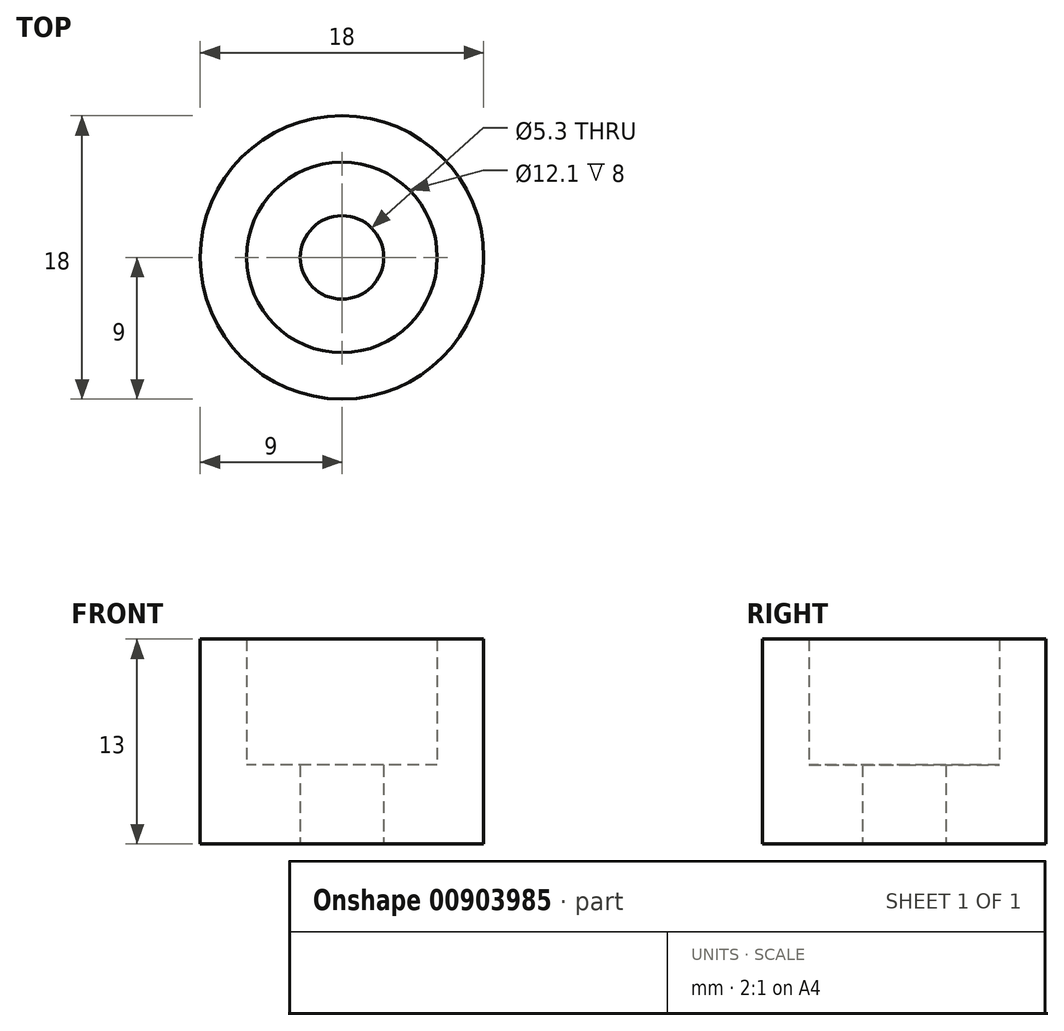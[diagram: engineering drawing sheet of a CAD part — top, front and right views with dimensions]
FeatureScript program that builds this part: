
annotation { "Feature Type Name" : "Feature", "Feature Type Description" : "" }
export const myFeature = defineFeature(function(context is Context, id is Id, definition is map)
    precondition{}
    {
        {
            var Q0;
            Q0=qCreatedBy(makeId("Top.planeOp"),FACE);
            var sketch = newSketch(context, id + "F0", { "sketchPlane" : qUnion([Q0])});
            skCircle(sketch, "E0", {"center": v(0, 0) * mm, "radius": 9 * mm});
            skCircle(sketch, "E1", {"center": v(0, 0) * mm, "radius": 6.05 * mm});
            skCircle(sketch, "E2", {"center": v(0, 0) * mm, "radius": 10 * mm});
            skCircle(sketch, "E3", {"center": v(0, 0) * mm, "radius": 2.65 * mm});
            skSolve(sketch);
        }
        {
            var Q0;
            Q0=makeQuery(id+"F0.imprint","IMPRINT",FACE,{"disambiguationData":[TD([[makeQuery(id+"F0.imprint","IMPRINT",EDGE,{"derivedFrom":sQuery(id+"F0.wireOp",EDGE,"E0")}),1.0]])]});
            var Q1;
            Q1=makeQuery(id+"F0.imprint","IMPRINT",FACE,{"disambiguationData":[TD([[makeQuery(id+"F0.imprint","IMPRINT",EDGE,{"derivedFrom":sQuery(id+"F0.wireOp",EDGE,"E1")}),1.0]])]});
            var Q2;
            Q2=makeQuery(id+"F0.imprint","IMPRINT",FACE,{"disambiguationData":[TD([[makeQuery(id+"F0.imprint","IMPRINT",EDGE,{"derivedFrom":sQuery(id+"F0.wireOp",EDGE,"E1")}),-1.0]])]});
            extrude(context, id + "F1", {"entities" : qUnion([Q0, Q1, Q2]), "depth" : 5 * mm, "offsetDistance" : 25 * mm});
        }
        {
            var Q0;
            Q0=makeQuery(id+"F0.imprint","IMPRINT",FACE,{"disambiguationData":[TD([[makeQuery(id+"F0.imprint","IMPRINT",EDGE,{"derivedFrom":sQuery(id+"F0.wireOp",EDGE,"E1")}),-1.0]])]});
            extrude(context, id + "F2", {"entities" : qUnion([Q0]), "operationType" : NewBodyOperationType.ADD, "depth" : 13 * mm, "offsetDistance" : 25 * mm});
        }
    });
